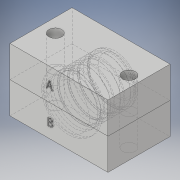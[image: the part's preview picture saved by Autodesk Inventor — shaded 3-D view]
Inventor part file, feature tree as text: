
AUTODESK INVENTOR PART (.ipt)
format: ipt  version: 2019.3 (Build 233278000, 278)  size: 350,208 bytes
history: native  units: mm
features: sketch x5, other x4, extrude x3, fillet x2, revolve x1, pattern_linear x1, emboss x1, hole x1, boolean_combine x1, split x1
ambient origin geometry x8: Origin, YZ Plane, XZ Plane, XY Plane, X Axis, Y Axis, Z Axis, Center Point
bodies: Body1 (feature_tree), Body2 (feature_tree)
feature tree (20):
  other  "Cap"
  sketch  "Sketch1"  dims[d0=22.225mm d1=19.0mm]
  extrude  "Extrusion1"  Depth=19.0mm
  extrude  "Extrusion2"  Depth=20.0mm TaperAngle=0.0deg
  revolve  "Revolution2"  [1 undecoded]
  fillet  "Fillet1"  Radius=40.0mm
  pattern_linear  "Rectangular Pattern1"  Spacing1=25.0mm  [1 undecoded]
  fillet  "Fillet2"  Radius=0.5mm
  extrude  "Extrusion3"  [1 undecoded]
  emboss  "Emboss1"
  hole  "Hole1"  [1 undecoded]
  boolean_combine  "Combine1"
  split  "Split1"
  sketch  "Sketch2"  dims[d2=3.0mm d3=0.0mm d4=20.0mm d5=0.0mm]
  sketch  "Sketch3"  dims[d7=90.0deg d9=2.0mm d10=40.0mm d12=4.0mm]
  other  "Mould"
  sketch  "Sketch4"  dims[d13=0.5mm]
  sketch  "Sketch6"  dims[d14=2.0mm d15=25.0mm d16=0.0mm d18=5.1mm d19=6.0mm d20=4.0mm d21=2.0mm d22=90.0deg d23=8.0mm d24=20.594885mm d25=0.5mm d26=0.0mm]
  other  "7_8-Cap-MoldA"
  other  "7_8-Cap-MoldB"
note: 4 required parameter values undecoded (feature->parameter linkage not recoverable at this tier; creation-order binding heuristic only, values carry confidence <= 0.55)